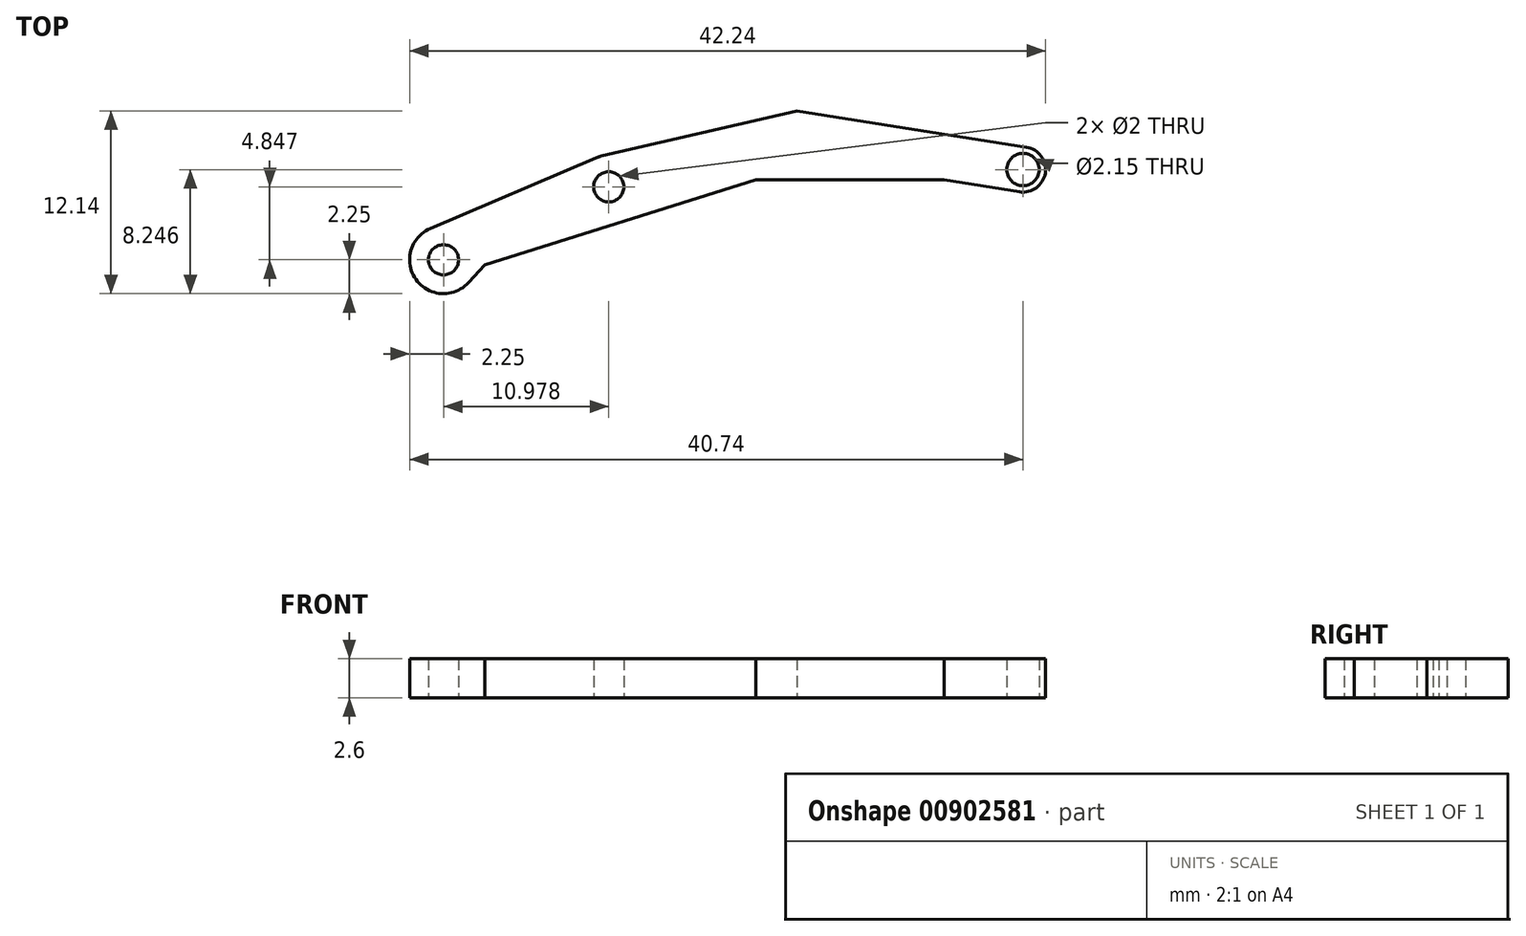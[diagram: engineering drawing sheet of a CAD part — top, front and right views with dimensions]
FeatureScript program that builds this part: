
annotation { "Feature Type Name" : "Feature", "Feature Type Description" : "" }
export const myFeature = defineFeature(function(context is Context, id is Id, definition is map)
    precondition{}
    {
        {
            var Q0;
            Q0=qCreatedBy(makeId("Top.planeOp"),FACE);
            var sketch = newSketch(context, id + "F0", { "sketchPlane" : qUnion([Q0])});
            skCircle(sketch, "E0", {"center": v(-3.92, 2.88) * mm, "radius": 2.1 * mm});
            skCircle(sketch, "E1", {"center": v(-14.9, -1.97) * mm, "radius": 2.25 * mm});
            skCircle(sketch, "E2", {"center": v(23.6, 4.03) * mm, "radius": 1.5 * mm});
            skLineSegment(sketch, "E3", {"start": v(-4.4, 4.92) * mm, "end": v(8.58, 7.92) * mm});
            skLineSegment(sketch, "E4", {"start": v(-4.75, 4.8) * mm, "end": v(-16.02, 0) * mm});
            skLineSegment(sketch, "E5", {"start": v(5.85, 3.33) * mm, "end": v(18.37, 3.33) * mm});
            skCircle(sketch, "E6", {"center": v(23.6, 4.03) * mm, "radius": 1.07 * mm});
            skCircle(sketch, "E7", {"center": v(-3.92, 2.88) * mm, "radius": 1 * mm});
            skCircle(sketch, "E8", {"center": v(-14.9, -1.97) * mm, "radius": 1 * mm});
            skLineSegment(sketch, "E9", {"start": v(-13.24, -3.49) * mm, "end": v(-12.16, -2.3) * mm});
            skLineSegment(sketch, "E10", {"start": v(-12.16, -2.3) * mm, "end": v(5.85, 3.33) * mm});
            skLineSegment(sketch, "E11", {"start": v(18.37, 3.33) * mm, "end": v(23.36, 2.54) * mm});
            skLineSegment(sketch, "E12", {"start": v(8.58, 7.92) * mm, "end": v(23.82, 5.5) * mm});
            skSolve(sketch);
        }
        {
            var Q0;
            Q0 = qSketchRegion(id + "F0", true);
            extrude(context, id + "F1", {"entities" : qUnion([Q0]), "depth" : 2.6 * mm, "offsetDistance" : 25 * mm});
        }
    });
